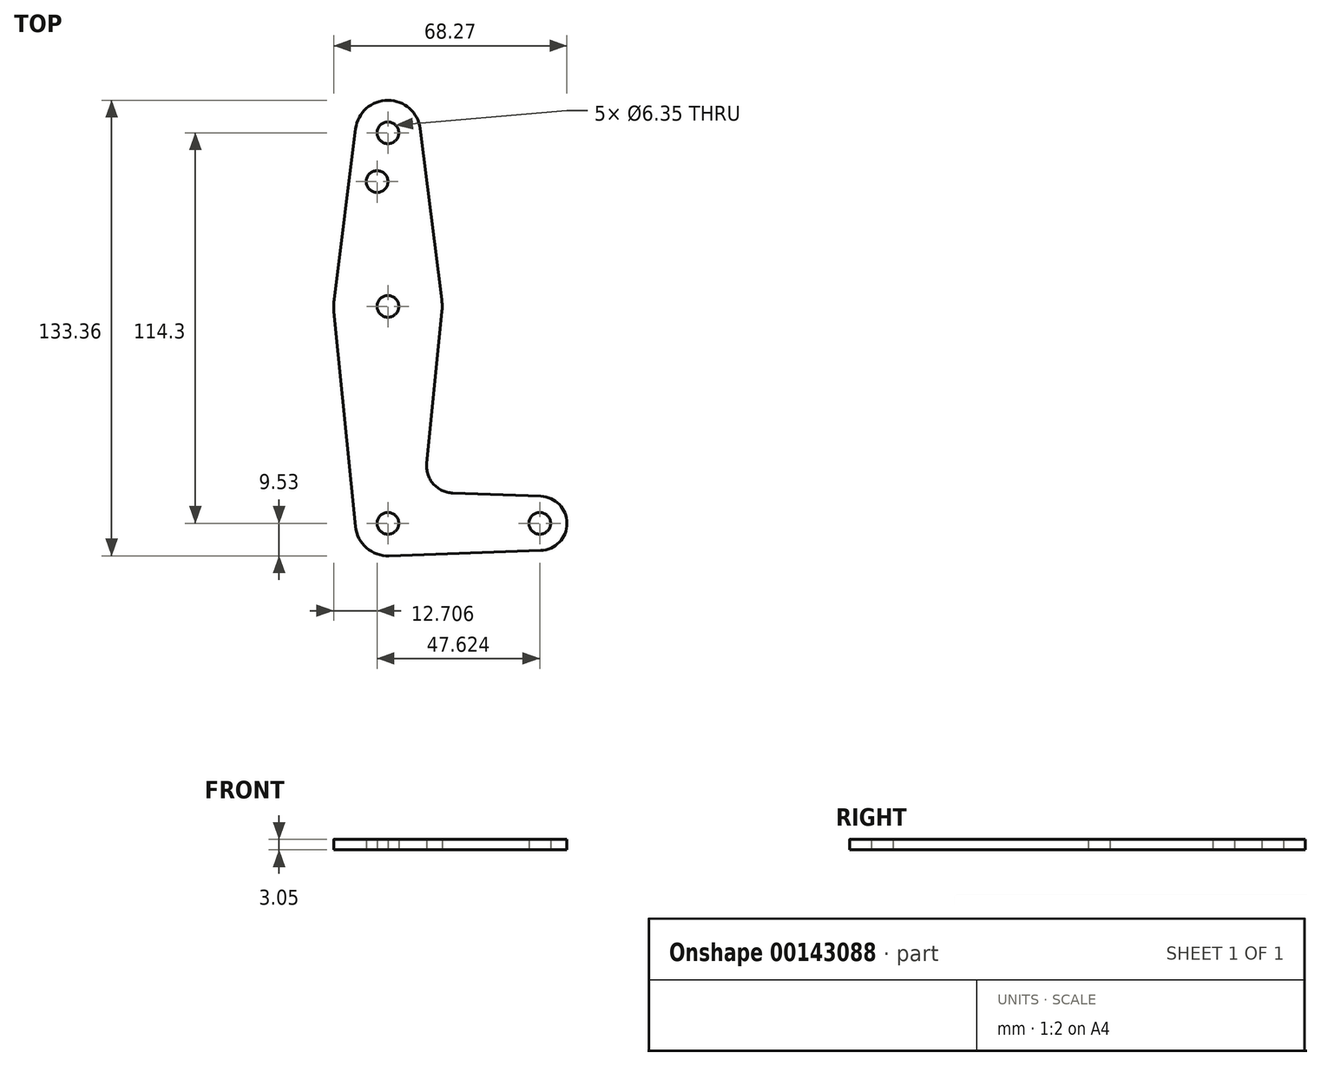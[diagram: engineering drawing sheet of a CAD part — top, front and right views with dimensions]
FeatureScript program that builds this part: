
annotation { "Feature Type Name" : "Feature", "Feature Type Description" : "" }
export const myFeature = defineFeature(function(context is Context, id is Id, definition is map)
    precondition{}
    {
        {
            var Q0;
            Q0=qCreatedBy(makeId("Top.planeOp"),FACE);
            var sketch = newSketch(context, id + "F0", { "sketchPlane" : qUnion([Q0])});
            skCircle(sketch, "E0", {"center": v(0, 114.3) * mm, "radius": 9.53 * mm});
            skCircle(sketch, "E1", {"center": v(0, 63.5) * mm, "radius": 15.88 * mm});
            skCircle(sketch, "E2", {"center": v(0, 0) * mm, "radius": 9.53 * mm});
            skCircle(sketch, "E3", {"center": v(44.45, 0) * mm, "radius": 7.94 * mm});
            skLineSegment(sketch, "E4", {"start": v(0, 114.3) * mm, "end": v(0, 0) * mm, "construction": true});
            skLineSegment(sketch, "E5", {"start": v(44.8, 7.93) * mm, "end": v(18.97, 8.85) * mm});
            skLineSegment(sketch, "E6", {"start": v(44.75, -7.93) * mm, "end": v(0, -9.53) * mm});
            skLineSegment(sketch, "E7", {"start": v(0, 0) * mm, "end": v(44.45, 0) * mm, "construction": true});
            skLineSegment(sketch, "E8", {"start": v(-15.8, 61.91) * mm, "end": v(-9.48, -0.95) * mm});
            skLineSegment(sketch, "E9", {"start": v(15.8, 61.91) * mm, "end": v(11.34, 17.6) * mm});
            skLineSegment(sketch, "E10", {"start": v(-9.45, 115.5) * mm, "end": v(-15.75, 65.48) * mm});
            skLineSegment(sketch, "E11", {"start": v(9.45, 115.5) * mm, "end": v(15.75, 65.48) * mm});
            skCircle(sketch, "E12", {"center": v(0, 114.3) * mm, "radius": 3.17 * mm});
            skCircle(sketch, "E13", {"center": v(0, 63.5) * mm, "radius": 3.17 * mm});
            skCircle(sketch, "E14", {"center": v(0, 0) * mm, "radius": 3.17 * mm});
            skCircle(sketch, "E15", {"center": v(44.45, 0) * mm, "radius": 3.17 * mm});
            skCircle(sketch, "E16", {"center": v(-3.17, 100.03) * mm, "radius": 3.17 * mm});
            skArc(sketch, "E17.filletArc", {"start": v(11.34, 17.6) * mm, "mid": v(13.26, 11.57) * mm, "end": v(18.97, 8.85) * mm});
            skSolve(sketch);
        }
        {
            var Q0;
            Q0=makeQuery(id+"F0.imprint","IMPRINT",FACE,{"disambiguationData":[TD([[makeQuery(id+"F0.imprint","IMPRINT",EDGE,{"derivedFrom":sQuery(id+"F0.wireOp",EDGE,"E13")}),-1.0]])]});
            var Q1;
            {var subQ6=sQuery(id+"F0.wireOp",EDGE,"E8");Q1=makeQuery(id+"F0.imprint","IMPRINT",FACE,{"disambiguationData":[TD([[makeQuery(id+"F0.imprint","IMPRINT",EDGE,{"derivedFrom":subQ6}),1.0]])]});}
            var Q2;
            Q2=makeQuery(id+"F0.imprint","IMPRINT",FACE,{"disambiguationData":[TD([[makeQuery(id+"F0.imprint","IMPRINT",EDGE,{"derivedFrom":sQuery(id+"F0.wireOp",EDGE,"E14")}),-1.0]])]});
            var Q3;
            Q3=makeQuery(id+"F0.imprint","IMPRINT",FACE,{"disambiguationData":[TD([[makeQuery(id+"F0.imprint","IMPRINT",EDGE,{"derivedFrom":sQuery(id+"F0.wireOp",EDGE,"E15")}),-1.0]])]});
            var Q4;
            {var subQ1=sQuery(id+"F0.wireOp",EDGE,"E10");Q4=makeQuery(id+"F0.imprint","IMPRINT",FACE,{"disambiguationData":[TD([[makeQuery(id+"F0.imprint","IMPRINT",EDGE,{"derivedFrom":subQ1}),1.0]])]});}
            var Q5;
            Q5=makeQuery(id+"F0.imprint","IMPRINT",FACE,{"disambiguationData":[TD([[makeQuery(id+"F0.imprint","IMPRINT",EDGE,{"derivedFrom":sQuery(id+"F0.wireOp",EDGE,"E12")}),-1.0]])]});
            extrude(context, id + "F1", {"entities" : qUnion([Q0, Q1, Q2, Q3, Q4, Q5]), "depth" : 3.05 * mm});
        }
    });
